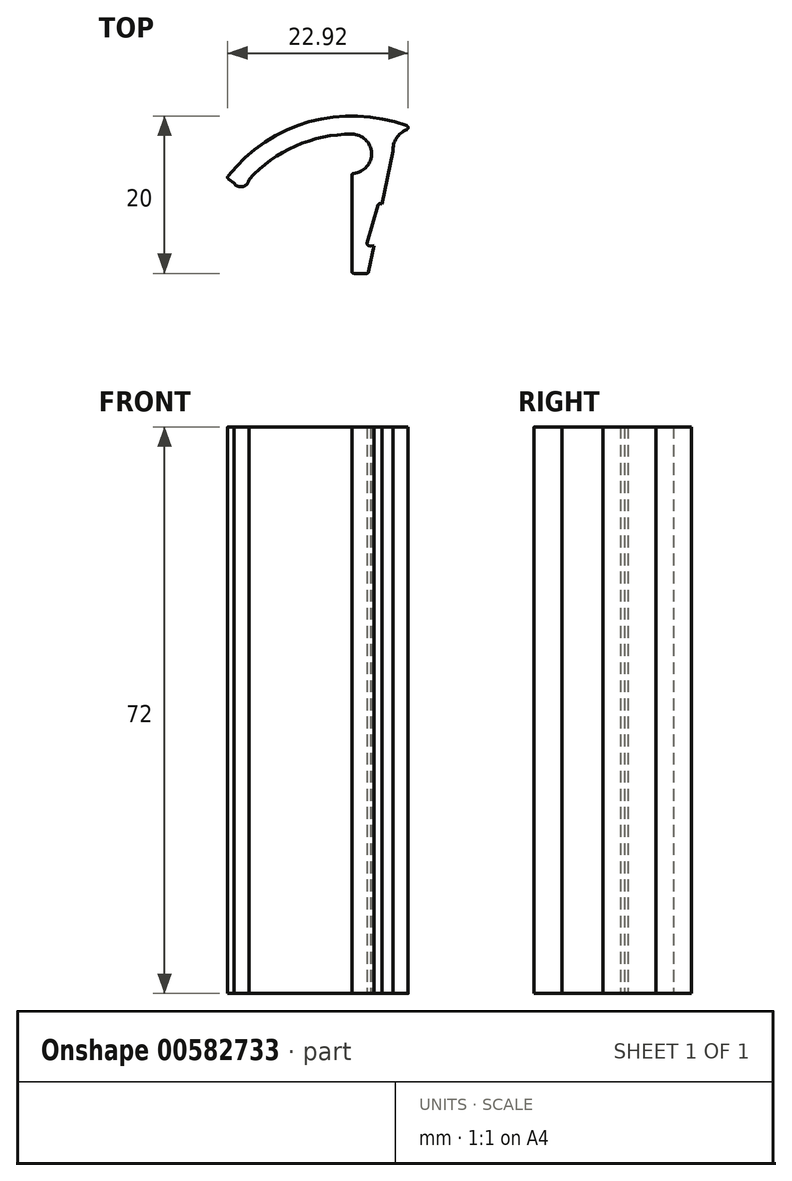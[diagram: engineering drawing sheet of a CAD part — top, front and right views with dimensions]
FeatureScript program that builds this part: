
annotation { "Feature Type Name" : "Feature", "Feature Type Description" : "" }
export const myFeature = defineFeature(function(context is Context, id is Id, definition is map)
    precondition{}
    {
        {
            var Q0;
            Q0=qCreatedBy(makeId("Top.planeOp"),FACE);
            var sketch = newSketch(context, id + "F0", { "sketchPlane" : qUnion([Q0])});
            skArc(sketch, "E0", {"start": v(6.98, 18.74) * mm, "mid": v(-5.42, 19.25) * mm, "end": v(-15.73, 12.36) * mm});
            skArc(sketch, "E1", {"start": v(5.47, 16.82) * mm, "mid": v(-4.53, 17.1) * mm, "end": v(-13.08, 11.9) * mm});
            skLineSegment(sketch, "E2", {"start": v(0, 0.25) * mm, "end": v(0, 12.44) * mm});
            skArc(sketch, "E3", {"start": v(0.23, 12.7) * mm, "mid": v(2.5, 15.3) * mm, "end": v(0, 17.68) * mm});
            skLineSegment(sketch, "E4", {"start": v(2.14, 0.2) * mm, "end": v(2.81, 3.55) * mm});
            skLineSegment(sketch, "E5", {"start": v(1.9, 0) * mm, "end": v(0.25, 0) * mm});
            skLineSegment(sketch, "E6", {"start": v(-14.97, 11.45) * mm, "end": v(-15.68, 12) * mm});
            skLineSegment(sketch, "E7", {"start": v(7.4, 18.34) * mm, "end": v(7.6, 18.5) * mm});
            skArc(sketch, "E8", {"start": v(6.99, 18.27) * mm, "mid": v(5.66, 17.17) * mm, "end": v(5.2, 15.51) * mm});
            skArc(sketch, "E9", {"start": v(-14.97, 11.45) * mm, "mid": v(-13.86, 11.02) * mm, "end": v(-13.08, 11.9) * mm});
            skPoint(sketch, "E10.visualSharp", {"position": v(-15.88, 12.16) * mm});
            skArc(sketch, "E10.filletArc", {"start": v(-15.73, 12.36) * mm, "mid": v(-15.78, 12.17) * mm, "end": v(-15.68, 12) * mm});
            skArc(sketch, "E11.filletArc", {"start": v(6.99, 18.27) * mm, "mid": v(7.14, 18.51) * mm, "end": v(6.98, 18.74) * mm});
            skPoint(sketch, "E12.visualSharp", {"position": v(0, 12.68) * mm});
            skArc(sketch, "E12.filletArc", {"start": v(0.23, 12.7) * mm, "mid": v(0.07, 12.61) * mm, "end": v(0, 12.44) * mm});
            skArc(sketch, "E13.filletArc", {"start": v(0, 0.25) * mm, "mid": v(0.07, 0.07) * mm, "end": v(0.25, 0) * mm});
            skPoint(sketch, "E14.visualSharp", {"position": v(2.1, 0) * mm});
            skArc(sketch, "E14.filletArc", {"start": v(1.9, 0) * mm, "mid": v(2.05, 0.06) * mm, "end": v(2.14, 0.2) * mm});
            skLineSegment(sketch, "E15.bottom", {"start": v(3.86, 8.77) * mm, "end": v(3.37, 8.9) * mm});
            skLineSegment(sketch, "E15.top", {"start": v(2.36, 3.48) * mm, "end": v(2.12, 3.54) * mm});
            skLineSegment(sketch, "E15.right", {"start": v(3.3, 8.66) * mm, "end": v(1.95, 3.85) * mm});
            skLineSegment(sketch, "E16", {"start": v(3.62, 8.83) * mm, "end": v(3.86, 8.77) * mm});
            skLineSegment(sketch, "E17", {"start": v(2.4, 3.6) * mm, "end": v(2.82, 3.59) * mm});
            skLineSegment(sketch, "E18.trimOffspring", {"start": v(3.86, 8.77) * mm, "end": v(5.2, 15.51) * mm});
            skPoint(sketch, "E19.start.orphan", {"position": v(7.05, 3.48) * mm});
            skLineSegment(sketch, "E20.trimOffspring", {"start": v(2.81, 3.55) * mm, "end": v(2.36, 3.48) * mm});
            skPoint(sketch, "E21.start.orphan", {"position": v(3.13, 3.61) * mm});
            skPoint(sketch, "E22.visualSharp", {"position": v(3.37, 8.9) * mm});
            skArc(sketch, "E22.filletArc", {"start": v(3.62, 8.83) * mm, "mid": v(3.43, 8.81) * mm, "end": v(3.3, 8.66) * mm});
            skPoint(sketch, "E23.visualSharp", {"position": v(1.88, 3.61) * mm});
            skArc(sketch, "E23.filletArc", {"start": v(1.95, 3.85) * mm, "mid": v(1.97, 3.66) * mm, "end": v(2.12, 3.54) * mm});
            skSolve(sketch);
        }
        {
            var Q0;
            Q0 = qSketchRegion(id + "F0", true);
            extrude(context, id + "F1", {"entities" : qUnion([Q0]), "flatOperationType" : FlatOperationType.REMOVE, "depth" : 72 * mm, "offsetDistance" : 25 * mm, "domain" : OperationDomain.MODEL});
        }
    });
